# Revit family: Haworth_Tijo_Lounge_Box_EU_PRELIMINARY
name_source: partatom
category: Furniture Systems
revit_build: Autodesk Revit 2018 (Build: 20170223_1515(x64)
units: mm (PartAtom-declared; Revit-internal decimal feet)

## family parameters
Always vertical = Yes
Cut with Voids When Loaded = No
OmniClass Number = 23.40.70.14.64.21
OmniClass Title = Systems Furniture
Part Type = Normal
Room Calculation Point = No
Round Connector Dimension = Use Diameter
Shared = No
Work Plane-Based = No

## types (6) — shared parameters
Actual Depth = 38 cm
Assembly Code = E2020200
Cushion Finish = Haworth _ Fabric _ Undecided _ Seating _ Lounge
Description = Haworth - Tijo - Lounge - Box
Manufacturer = Haworth
Model = TJXBX
Revision Number = 1
Size = Verify Final Dim. w/ Haworth
Trim Finish = Haworth _ Polymer _ Black
URL = https://www.haworth.com
URL - Product = https://www.haworth.com
Warranty = http://www.haworth.com

## per-type parameters (varying)
| type | Actual Height | Actual Width | Cushion | Double | Large | Single | Single Step |
| Single Step Box - with Cushion | 21 cm | 38 cm | Yes | No | No | No | Yes |
| Double Box - with Cushion | 41 cm | 76 cm | Yes | Yes | Yes | No | No |
| Single Box - with Cushion | 41 cm | 38 cm | Yes | No | Yes | Yes | No |
| Double Box - w/o Cushion | 41 cm | 76 cm | No | Yes | Yes | No | No |
| Single Box - w/o Cushion | 41 cm | 38 cm | No | No | Yes | Yes | No |
| Single Step Box - w/o Cushion | 21 cm | 38 cm | No | No | No | No | Yes |

## geometry (parser evidence)
native form markers: Sweep x9
no freeform markers — native parametric forms only
